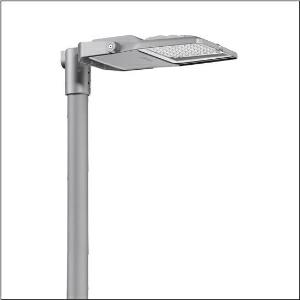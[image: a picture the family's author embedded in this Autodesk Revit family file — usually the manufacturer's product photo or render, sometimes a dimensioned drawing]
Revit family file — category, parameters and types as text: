
# Revit family: floodlight_fl_21_iq_mini___pl61_5xa7772d4c3a_23c5
name_source: partatom
category: Lighting Fixtures
units: mm (PartAtom-declared; Revit-internal decimal feet)

## family parameters
Cut with Voids When Loaded = No
Host = Face
Light Source = No
Part Type = Normal
Room Calculation Point = No
Round Connector Dimension = Use Diameter
Shared = No

## types (1)
- --- (1 x LED, 18260 lm, 143 W, 4000K)
    Apparent Load = 143 VA
    CIE Flux Codes = 33 65 98 100 100
    Color Rendering = 70
    Color Temperature = 4000K
    Default Elevation = 1800 mm
    Description = Floodlight FL 21 iQ mini, floodlight, primary light control with lens, of PMMA, primary optical cover: protective disc, of toughened safety glass, transparent, light distribution: PL61, light emission: direct distribution, installation type: surface-mounted, LED, High Power LED, rated luminous flux: 18.260lm, luminous efficacy: 128lm/W, light colour: 740, colour temperature: 4000K, control: Auto-Match, Temp-Guard, Night-Set, Smart-Wire, Desk-Remote (wireless, voltage-free reading and setting of iQ features in the workshop via application-optimized NFC function/RFID function), optimised constant luminous flux control (CLO 2.0), Light-Fading, Lumen-Switch, with terminal, 6-pole, mains connection: 220..240V, AC, 50/60Hz, start of lifetime: 143W, end of service life: 152W, reduction: 61W, luminaire housing, of diecast aluminium, powder-coated, Siteco® metallic grey (DB 702S), corrosivity category C5 mid according to DIN EN ISO 12944, sealing non-destructively replaceable, please order mast flange separately, mast bracket, of steel, galvanised, powder-coated, protection rating (complete): IP66, insulation class (complete): insulation class II (safety insulation), certification: CE, ENEC, VDE, protection symbol: D, impact resistance: IK08, permissible operating ambient temperature: -40..+40°C, permissible operating ambient temperature for outdoor applications: -40..+50°C, standard: DIN EN 12944, LABS conformity tested according to VDMA 24364:2018-05, packaging unit: 1 piece

Light Distribution: PL61
    Height = 70 mm
    Lamp = 1 x LED
    Lamp Light Flux = 18260 lm
    Lamp Power = 143 W
    Lamp count = 1
    Length = 485 mm
    Luminous efficacy = 128 lm/W
    Manufacturer = Siteco
    ModVariant = No
    Model = 5XA7772D4C3A
    Number of Poles = 1
    OnlyDefault = Yes
    Power Factor = 1
    Product Name = Floodlight FL 21 iQ mini | PL61
    Product group = floodlight | pylon annexe
    ProductGroupID = 6200
    Protection Class = Protection class II
    Protection Degree = IP 66
    RLX_Detail_Level = 1
    RLX_Emergency_Light_Flux = 0 lm
    RLX_Emergency_Type = 0
    RLX_Emergency_Type_DB = No
    RlxData = <blob elided: 101633 chars, md5=9701d00b>
    Socket = socket
    Standby Power = 0 W
    System Light Flux = 18260 lm
    System Power = 143 W
    Type Comments = factory setting: luminous flux: 100 % | dim-lin: 254 | 730 mA
    Type Image = l_1007125.jpg
    URL = http://relux.com
    VarID = @adj_123227
    Voltage = 0 V
    Weight = 0.00 kg
    Width = 337 mm

## geometry (parser evidence)
native form markers: Blend x4, Sweep x11
no freeform markers — native parametric forms only
